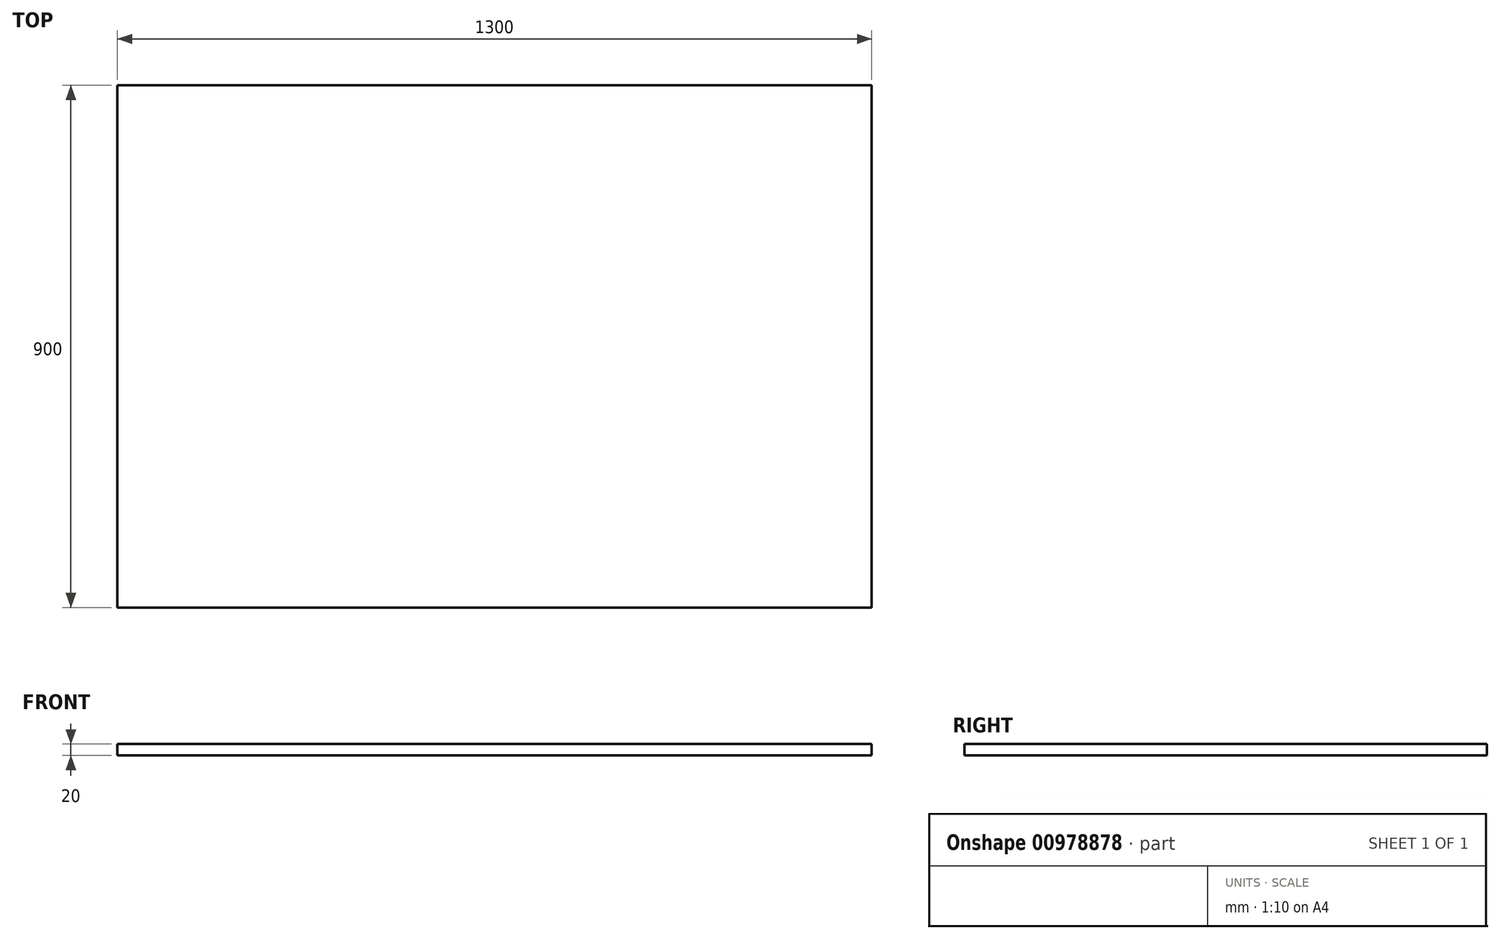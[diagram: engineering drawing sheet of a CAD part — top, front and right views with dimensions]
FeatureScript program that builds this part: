
annotation { "Feature Type Name" : "Feature", "Feature Type Description" : "" }
export const myFeature = defineFeature(function(context is Context, id is Id, definition is map)
    precondition{}
    {
        {
            var Q0;
            Q0=qCreatedBy(makeId("Top.planeOp"),FACE);
            var sketch = newSketch(context, id + "F0", { "sketchPlane" : qUnion([Q0])});
            skLineSegment(sketch, "E0.bottom", {"start": v(-670.7, 610.15) * mm, "end": v(629.3, 610.15) * mm});
            skLineSegment(sketch, "E0.top", {"start": v(-670.7, -289.85) * mm, "end": v(629.3, -289.85) * mm});
            skLineSegment(sketch, "E0.left", {"start": v(-670.7, 610.15) * mm, "end": v(-670.7, -289.85) * mm});
            skLineSegment(sketch, "E0.right", {"start": v(629.3, 610.15) * mm, "end": v(629.3, -289.85) * mm});
            skSolve(sketch);
        }
        {
            var Q0;
            Q0 = qSketchRegion(id + "F0", true);
            extrude(context, id + "F1", {"entities" : qUnion([Q0]), "depth" : 20 * mm, "offsetDistance" : 25 * mm});
        }
    });
